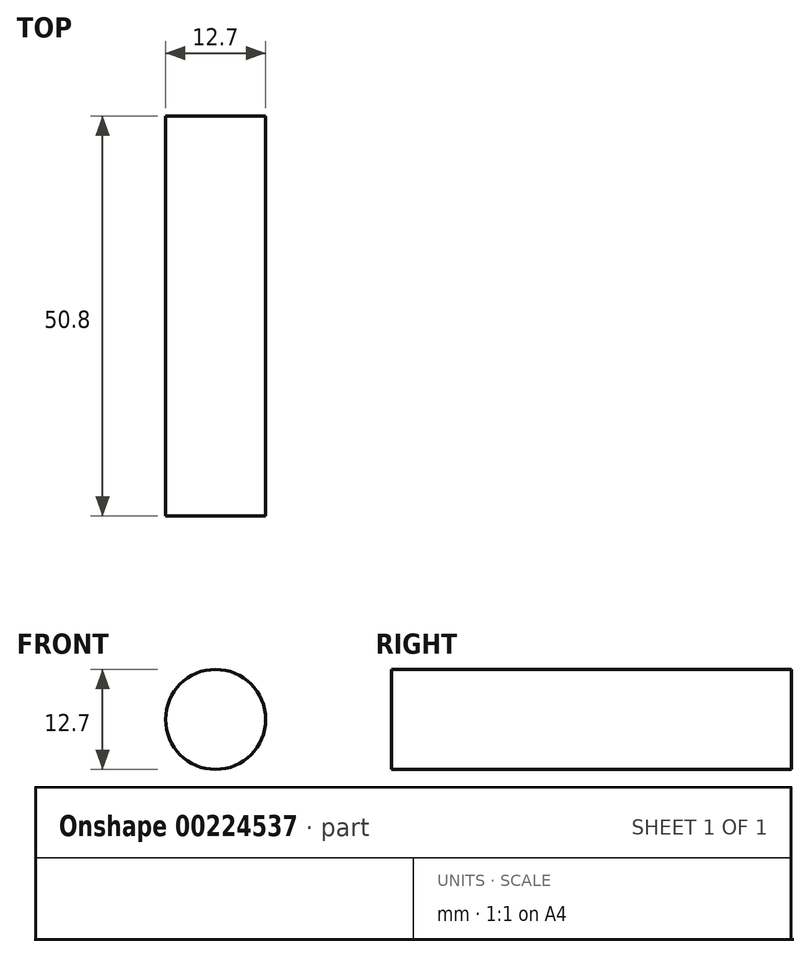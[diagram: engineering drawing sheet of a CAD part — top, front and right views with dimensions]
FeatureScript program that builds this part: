
annotation { "Feature Type Name" : "Feature", "Feature Type Description" : "" }
export const myFeature = defineFeature(function(context is Context, id is Id, definition is map)
    precondition{}
    {
        {
            var Q0;
            Q0=qCreatedBy(makeId("Front.planeOp"),FACE);
            var sketch = newSketch(context, id + "F0", { "sketchPlane" : qUnion([Q0])});
            skCircle(sketch, "E0", {"center": v(-46.72, 37.68) * mm, "radius": 6.35 * mm});
            skSolve(sketch);
        }
        {
            var Q0;
            Q0 = qSketchRegion(id + "F0", true);
            extrude(context, id + "F1", {"entities" : qUnion([Q0]), "depth" : 50.8 * mm});
        }
    });
